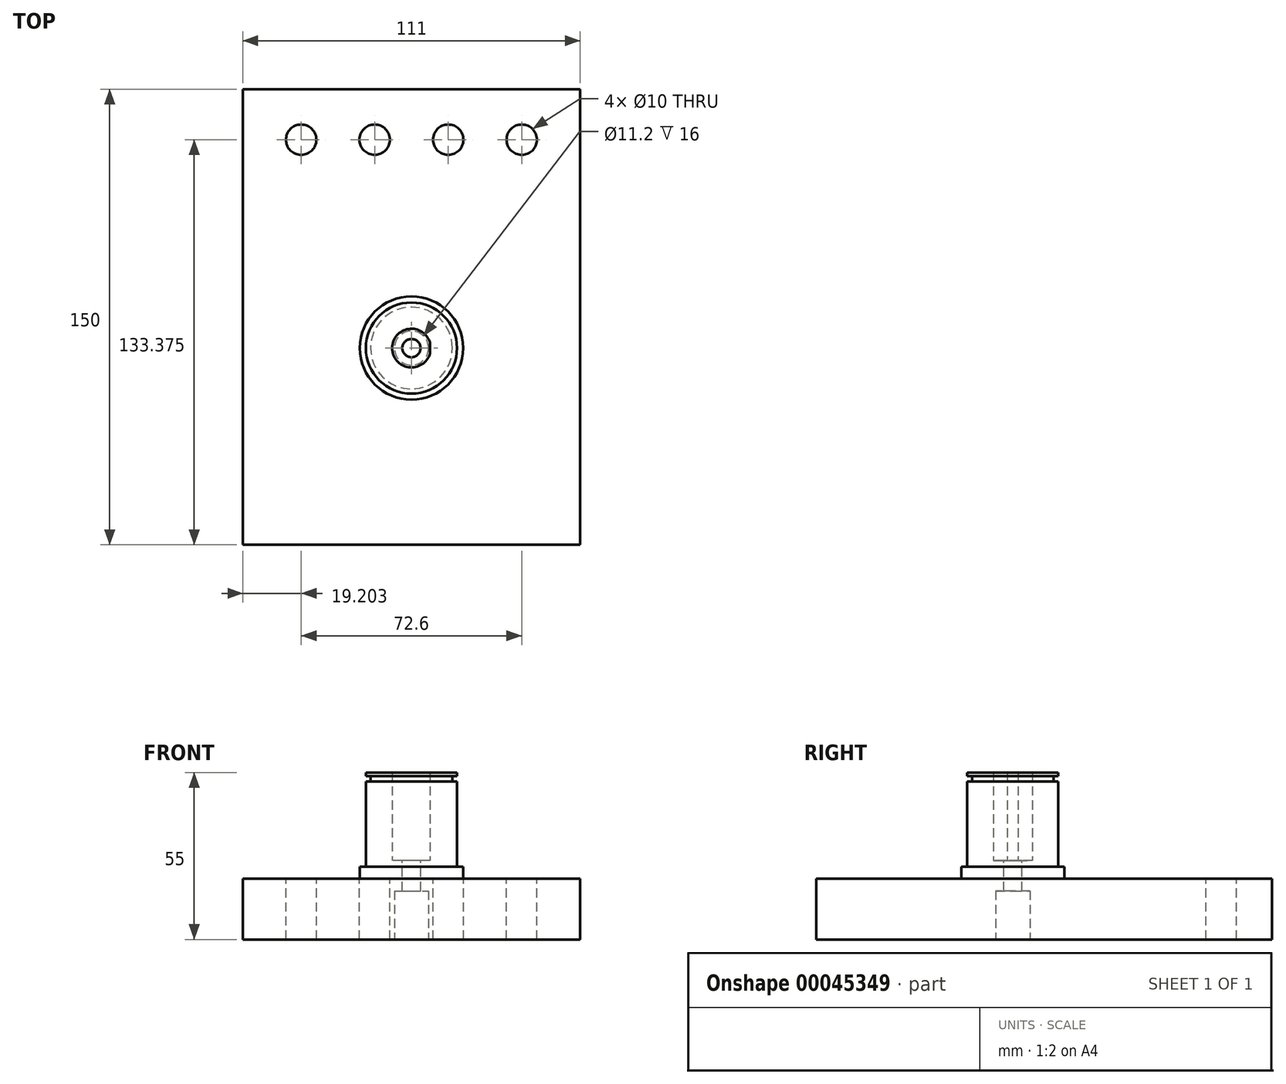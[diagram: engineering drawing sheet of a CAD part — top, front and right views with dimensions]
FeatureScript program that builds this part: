
annotation { "Feature Type Name" : "Feature", "Feature Type Description" : "" }
export const myFeature = defineFeature(function(context is Context, id is Id, definition is map)
    precondition{}
    {
        {
            var Q0;
            Q0=qCreatedBy(makeId("Front.planeOp"),FACE);
            var sketch = newSketch(context, id + "F0", { "sketchPlane" : qUnion([Q0])});
            skLineSegment(sketch, "E0.bottom", {"start": v(-54.84, -11.84) * mm, "end": v(56.16, -11.84) * mm});
            skLineSegment(sketch, "E0.top", {"start": v(-54.84, -31.84) * mm, "end": v(56.16, -31.84) * mm});
            skLineSegment(sketch, "E0.left", {"start": v(-54.84, -11.84) * mm, "end": v(-54.84, -31.84) * mm});
            skLineSegment(sketch, "E0.right", {"start": v(56.16, -11.84) * mm, "end": v(56.16, -31.84) * mm});
            skSolve(sketch);
        }
        {
            var Q0;
            Q0 = qSketchRegion(id + "F0", true);
            extrude(context, id + "F1", {"entities" : qUnion([Q0]), "depth" : 150 * mm});
        }
        {
            var Q0;
            Q0=makeQuery(id+"F1.opExtrude","SWEPT_FACE",FACE,{"disambiguationData":[OSD([sQuery(id+"F0.wireOp",EDGE,"E0.bottom")])]});
            var sketch = newSketch(context, id + "F2", { "sketchPlane" : qUnion([Q0])});
            skCircle(sketch, "E1", {"center": v(0.66, -85.25) * mm, "radius": 15 * mm});
            skArc(sketch, "E2", {"start": v(6.77, -83.47) * mm, "mid": v(-5.7, -85.25) * mm, "end": v(6.77, -87.03) * mm});
            skLineSegment(sketch, "E3.right", {"start": v(6.77, -83.47) * mm, "end": v(6.77, -87.03) * mm});
            skSolve(sketch);
        }
        {
            var Q0;
            Q0 = qSketchRegion(id + "F2", true);
            extrude(context, id + "F3", {"entities" : qUnion([Q0]), "operationType" : NewBodyOperationType.ADD, "depth" : 35 * mm});
        }
        {
            var Q0;
            Q0=makeQuery(id+"F3.opExtrude","CAP_FACE",FACE,{"disambiguationData":[OSD([sQuery(id+"F2.wireOp",EDGE,"E1"),sQuery(id+"F2.wireOp",EDGE,"E2")])],"isStart":false});
            var sketch = newSketch(context, id + "F4", { "sketchPlane" : qUnion([Q0])});
            skCircle(sketch, "E4", {"center": v(0.66, -85.25) * mm, "radius": 13.45 * mm});
            skCircle(sketch, "E5", {"center": v(0.66, -85.25) * mm, "radius": 15 * mm});
            skSolve(sketch);
        }
        {
            var Q0;
            Q0 = qSketchRegion(id + "F4", true);
            extrude(context, id + "F5", {"entities" : qUnion([Q0]), "operationType" : NewBodyOperationType.REMOVE, "oppositeDirection" : true, "depth" : 3 * mm});
        }
        {
            var Q0;
            Q0=makeQuery(id+"F3.opExtrude","CAP_FACE",FACE,{"disambiguationData":[OSD([sQuery(id+"F2.wireOp",EDGE,"E1"),sQuery(id+"F2.wireOp",EDGE,"E2")])],"isStart":false});
            var sketch = newSketch(context, id + "F6", { "sketchPlane" : qUnion([Q0])});
            skCircle(sketch, "E6", {"center": v(0.66, -85.25) * mm, "radius": 15 * mm});
            skCircle(sketch, "E7", {"center": v(0.66, -85.25) * mm, "radius": 13.45 * mm});
            skSolve(sketch);
        }
        {
            var Q0;
            Q0 = qSketchRegion(id + "F6", true);
            extrude(context, id + "F7", {"entities" : qUnion([Q0]), "operationType" : NewBodyOperationType.ADD, "oppositeDirection" : true, "depth" : 1.22 * mm});
        }
        {
            var Q0;
            {var subQ1=sQuery(id+"F0.wireOp",EDGE,"E0.left");var subQ3=sQuery(id+"F0.wireOp",EDGE,"E0.bottom");Q0=makeQuery(id+"F3.boolean.opBoolean","SPLIT",FACE,{"disambiguationData":[TD([makeQuery(id+"F1.opExtrude","SWEPT_FACE",FACE,{"disambiguationData":[OSD([subQ1])]})])],"derivedFrom":makeQuery(id+"F1.opExtrude","SWEPT_FACE",FACE,{"disambiguationData":[OSD([subQ3])]})});}
            var sketch = newSketch(context, id + "F8", { "sketchPlane" : qUnion([Q0])});
            skCircle(sketch, "E8", {"center": v(0.66, -85.25) * mm, "radius": 17 * mm});
            skSolve(sketch);
        }
        {
            var Q0;
            Q0 = qSketchRegion(id + "F8", true);
            extrude(context, id + "F9", {"entities" : qUnion([Q0]), "operationType" : NewBodyOperationType.ADD, "depth" : 4 * mm});
        }
        {
            var Q0;
            Q0=makeQuery(id+"F9.boolean.opBoolean","SPLIT",FACE,{"disambiguationData":[TD([makeQuery(id+"F3.opExtrude","SWEPT_FACE",FACE,{"disambiguationData":[OSD([sQuery(id+"F2.wireOp",EDGE,"E2")])]})])],"derivedFrom":makeQuery(id+"F9.opExtrude","CAP_FACE",FACE,{"disambiguationData":[OSD([sQuery(id+"F8.wireOp",EDGE,"E8")])],"isStart":false})});
            var sketch = newSketch(context, id + "F10", { "sketchPlane" : qUnion([Q0])});
            skCircle(sketch, "E9", {"center": v(0.66, -85.25) * mm, "radius": 8.54 * mm});
            skSolve(sketch);
        }
        {
            var Q0;
            Q0 = qSketchRegion(id + "F10", true);
            extrude(context, id + "F11", {"entities" : qUnion([Q0]), "operationType" : NewBodyOperationType.ADD, "depth" : 2 * mm});
        }
        {
            var Q0;
            {var subQ1=sQuery(id+"F0.wireOp",EDGE,"E0.left");var subQ3=sQuery(id+"F0.wireOp",EDGE,"E0.bottom");Q0=makeQuery(id+"F3.boolean.opBoolean","SPLIT",FACE,{"disambiguationData":[TD([makeQuery(id+"F1.opExtrude","SWEPT_FACE",FACE,{"disambiguationData":[OSD([subQ1])]})])],"derivedFrom":makeQuery(id+"F1.opExtrude","SWEPT_FACE",FACE,{"disambiguationData":[OSD([subQ3])]})});}
            var sketch = newSketch(context, id + "F12", { "sketchPlane" : qUnion([Q0])});
            skCircle(sketch, "E10", {"center": v(36.96, -16.62) * mm, "radius": 5 * mm});
            skCircle(sketch, "E11.1.0.0", {"center": v(12.76, -16.62) * mm, "radius": 5 * mm});
            skCircle(sketch, "E11.2.0.0", {"center": v(-11.44, -16.62) * mm, "radius": 5 * mm});
            skCircle(sketch, "E11.3.0.0", {"center": v(-35.64, -16.62) * mm, "radius": 5 * mm});
            skLineSegment(sketch, "E11.direction1", {"start": v(36.96, -16.62) * mm, "end": v(12.76, -16.62) * mm, "construction": true});
            skSolve(sketch);
        }
        {
            var Q0;
            Q0 = qSketchRegion(id + "F12", true);
            extrude(context, id + "F13", {"entities" : qUnion([Q0]), "operationType" : NewBodyOperationType.REMOVE, "endBound" : BoundingType.THROUGH_ALL, "oppositeDirection" : true, "depth" : 25 * mm});
        }
        {
            var Q0;
            Q0=makeQuery(id+"F11.opExtrude","CAP_FACE",FACE,{"disambiguationData":[OSD([sQuery(id+"F10.wireOp",EDGE,"E9")])],"isStart":false});
            var sketch = newSketch(context, id + "F14", { "sketchPlane" : qUnion([Q0])});
            skCircle(sketch, "E12", {"center": v(0.66, -85.25) * mm, "radius": 3 * mm});
            skSolve(sketch);
        }
        {
            var Q0;
            Q0 = qSketchRegion(id + "F14", true);
            extrude(context, id + "F15", {"entities" : qUnion([Q0]), "operationType" : NewBodyOperationType.REMOVE, "endBound" : BoundingType.THROUGH_ALL, "oppositeDirection" : true, "depth" : 25 * mm});
        }
        {
            var Q0;
            Q0=makeQuery(id+"F1.opExtrude","SWEPT_FACE",FACE,{"disambiguationData":[OSD([sQuery(id+"F0.wireOp",EDGE,"E0.top")])]});
            var sketch = newSketch(context, id + "F16", { "sketchPlane" : qUnion([Q0])});
            skCircle(sketch, "E13", {"center": v(0.66, 85.25) * mm, "radius": 5.6 * mm});
            skSolve(sketch);
        }
        {
            var Q0;
            Q0 = qSketchRegion(id + "F16", true);
            extrude(context, id + "F17", {"entities" : qUnion([Q0]), "operationType" : NewBodyOperationType.REMOVE, "oppositeDirection" : true, "depth" : 16 * mm});
        }
    });
